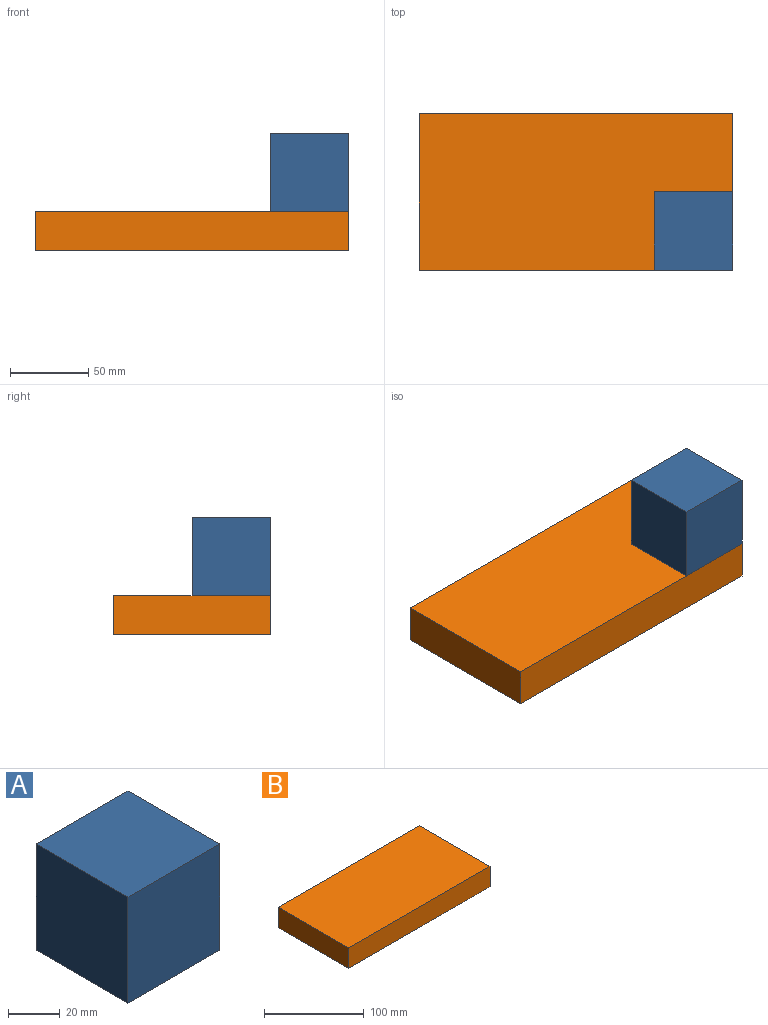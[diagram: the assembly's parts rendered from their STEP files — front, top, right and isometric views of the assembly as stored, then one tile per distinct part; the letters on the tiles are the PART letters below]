
ASSEMBLY  parts=2 mates=1
PART A: 6 faces, bbox 50x50x50 mm
  f0: plane 50x50mm, normal (1,0,0), area 2500mm2, adj f1,f3,f4,f5
  f1: plane 50x50mm, normal (0,1,0), area 2500mm2, adj f0,f2,f4,f5
  f2: plane 50x50mm, normal (-1,0,0), area 2500mm2, adj f1,f3,f4,f5
  f3: plane 50x50mm, normal (0,-1,0), area 2500mm2, adj f0,f2,f4,f5
  f4: plane 50x50mm, normal (0,0,1), area 2500mm2, adj f0,f1,f2,f3
  f5: plane 50x50mm, normal (0,0,-1), area 2500mm2, adj f0,f1,f2,f3
PART B: 6 faces, bbox 200x100x25 mm
  f0: plane 100x25mm, normal (1,0,0), area 2500mm2, adj f1,f3,f4,f5
  f1: plane 200x25mm, normal (0,1,0), area 5000mm2, adj f0,f2,f4,f5
  f2: plane 100x25mm, normal (-1,0,0), area 2500mm2, adj f1,f3,f4,f5
  f3: plane 200x25mm, normal (0,-1,0), area 5000mm2, adj f0,f2,f4,f5
  f4: plane 200x100mm, normal (0,0,1), area 20000mm2, adj f0,f1,f2,f3
  f5: plane 200x100mm, normal (0,0,-1), area 20000mm2, adj f0,f1,f2,f3
PLACE A t=(83.95,-9.14,28.66)mm
PLACE B t=(8.95,15.86,3.66)mm
MATE fastened A.f5 <-> B.f4  axis (0,0,-1) through (108.95,-34.14,28.66)mm
